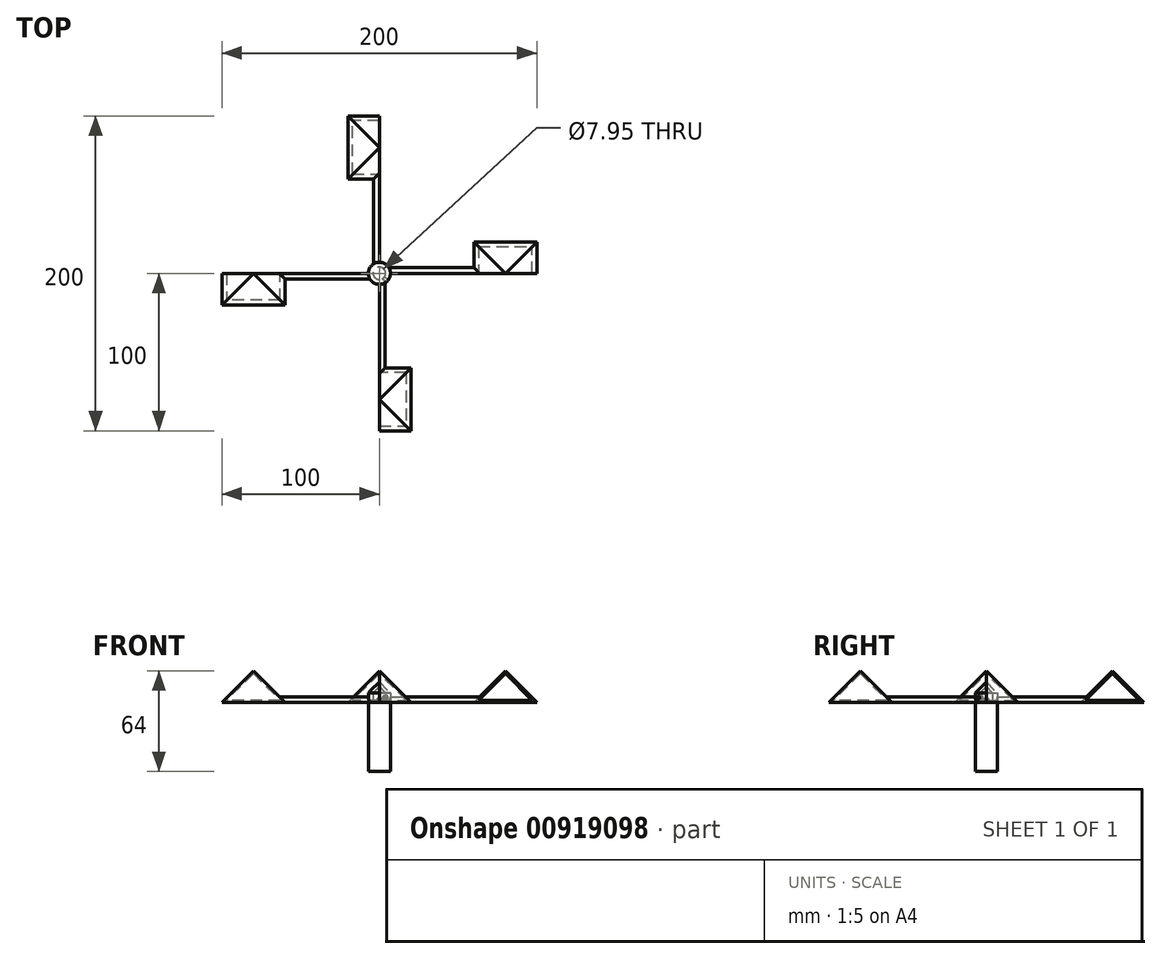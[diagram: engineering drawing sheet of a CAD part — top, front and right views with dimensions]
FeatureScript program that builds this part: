
annotation { "Feature Type Name" : "Feature", "Feature Type Description" : "" }
export const myFeature = defineFeature(function(context is Context, id is Id, definition is map)
    precondition{}
    {
        {
            var Q0;
            Q0=qCreatedBy(makeId("Front.planeOp"),FACE);
            var sketch = newSketch(context, id + "F0", { "sketchPlane" : qUnion([Q0])});
            skLineSegment(sketch, "E0.bottom", {"start": v(3.98, 0) * mm, "end": v(7, 0) * mm});
            skLineSegment(sketch, "E0.top", {"start": v(3.97, 6) * mm, "end": v(7, 6) * mm});
            skLineSegment(sketch, "E0.left", {"start": v(3.98, 0) * mm, "end": v(3.97, 6) * mm});
            skLineSegment(sketch, "E0.right", {"start": v(7, 0) * mm, "end": v(7, 6) * mm});
            skLineSegment(sketch, "E1", {"start": v(0, 0) * mm, "end": v(0, 6) * mm, "construction": true});
            skLineSegment(sketch, "E2.bottom", {"start": v(3.97, 0) * mm, "end": v(60, 0) * mm});
            skLineSegment(sketch, "E2.top", {"start": v(3.97, 3.6) * mm, "end": v(60, 3.6) * mm});
            skLineSegment(sketch, "E2.left", {"start": v(3.98, 0) * mm, "end": v(3.98, 3.6) * mm});
            skLineSegment(sketch, "E2.right", {"start": v(60, 0) * mm, "end": v(60, 3.6) * mm});
            skLineSegment(sketch, "E3.bottom", {"start": v(100, -20) * mm, "end": v(60, -20) * mm});
            skLineSegment(sketch, "E3.top", {"start": v(100, 20) * mm, "end": v(60, 20) * mm});
            skLineSegment(sketch, "E3.left", {"start": v(100, -20) * mm, "end": v(100, 20) * mm});
            skLineSegment(sketch, "E3.right", {"start": v(60, -20) * mm, "end": v(60, 20) * mm});
            skPoint(sketch, "E3.middle", {"position": v(80, 0) * mm});
            skLineSegment(sketch, "E4", {"start": v(60, 0) * mm, "end": v(100, 0) * mm});
            skLineSegment(sketch, "E5", {"start": v(60, 0) * mm, "end": v(63.6, 3.6) * mm});
            skLineSegment(sketch, "E6", {"start": v(63.6, 3.6) * mm, "end": v(60, 3.6) * mm});
            skLineSegment(sketch, "E7", {"start": v(3.97, 6) * mm, "end": v(0, 9.97) * mm});
            skLineSegment(sketch, "E8", {"start": v(0, 9.97) * mm, "end": v(0, 13) * mm});
            skLineSegment(sketch, "E9", {"start": v(0, 13) * mm, "end": v(7, 6) * mm});
            skSolve(sketch);
        }
        {
            var Q0;
            {var subQ2=sQuery(id+"F0.wireOp",EDGE,"E3.top");Q0=makeQuery(id+"F0.imprint","IMPRINT",FACE,{"disambiguationData":[TD([[makeQuery(id+"F0.imprint","IMPRINT",EDGE,{"derivedFrom":subQ2}),1.0]])]});}
            var Q1;
            Q1=makeQuery(id+"F0.imprint","IMPRINT",FACE,{"disambiguationData":[TD([[makeQuery(id+"F0.imprint","IMPRINT",EDGE,{"derivedFrom":sQuery(id+"F0.wireOp",EDGE,"E2.right")}),-1.0]])]});
            extrude(context, id + "F1", {"entities" : qUnion([Q0, Q1]), "oppositeDirection" : true, "depth" : 20 * mm, "offsetDistance" : 25 * mm});
        }
        {
            var Q0;
            Q0=makeQuery(id+"F1.opExtrude","SWEPT_EDGE",EDGE,{"disambiguationData":[OSD([sQuery(id+"F0.wireOp",EDGE,"E3.top"),sQuery(id+"F0.wireOp",EDGE,"E3.right")])]});
            var Q1;
            Q1=makeQuery(id+"F1.opExtrude","CAP_EDGE",EDGE,{"disambiguationData":[OSD([sQuery(id+"F0.wireOp",EDGE,"E3.top")])],"isStart":false});
            var Q2;
            Q2=makeQuery(id+"F1.opExtrude","SWEPT_EDGE",EDGE,{"disambiguationData":[OSD([sQuery(id+"F0.wireOp",EDGE,"E3.top"),sQuery(id+"F0.wireOp",EDGE,"E3.left")])]});
            chamfer(context, id + "F2", {"entities" : qUnion([Q0, Q1, Q2]), "width" : 20 * mm, "tangentPropagation" : true});
        }
        {
            var Q0;
            Q0=makeQuery(id+"F1.opExtrude","CAP_FACE",FACE,{"disambiguationData":[OSD([sQuery(id+"F0.wireOp",EDGE,"E2.right"),sQuery(id+"F0.wireOp",EDGE,"E3.top"),sQuery(id+"F0.wireOp",EDGE,"E3.left"),sQuery(id+"F0.wireOp",EDGE,"E3.right"),sQuery(id+"F0.wireOp",EDGE,"E4")])],"isStart":true});
            shell(context, id + "F3", {"entities" : qUnion([Q0]), "thickness" : 1.2 * mm});
        }
        {
            var Q0;
            {var subQ0=sQuery(id+"F0.wireOp",EDGE,"E2.bottom");Q0=makeQuery(id+"F0.imprint","IMPRINT",FACE,{"disambiguationData":[TD([[makeQuery(id+"F0.imprint","IMPRINT",EDGE,{"derivedFrom":subQ0}),1.0]])]});}
            var Q1;
            Q1=makeQuery(id+"F0.imprint","IMPRINT",FACE,{"disambiguationData":[TD([[makeQuery(id+"F0.imprint","IMPRINT",EDGE,{"derivedFrom":sQuery(id+"F0.wireOp",EDGE,"E2.right")}),-1.0]])]});
            var Q2;
            {var subQ0=sQuery(id+"F0.wireOp",EDGE,"E0.bottom");Q2=makeQuery(id+"F0.imprint","IMPRINT",FACE,{"disambiguationData":[TD([[makeQuery(id+"F0.imprint","IMPRINT",EDGE,{"derivedFrom":subQ0}),1.0]])]});}
            extrude(context, id + "F4", {"entities" : qUnion([Q0, Q1, Q2]), "operationType" : NewBodyOperationType.ADD, "oppositeDirection" : true, "depth" : 5 * mm, "offsetDistance" : 25 * mm});
        }
        {
            var Q0;
            {var subQ0=sQuery(id+"F0.wireOp",EDGE,"E0.top");Q0=makeQuery(id+"F0.imprint","IMPRINT",FACE,{"disambiguationData":[TD([[makeQuery(id+"F0.imprint","IMPRINT",EDGE,{"derivedFrom":subQ0}),-1.0]])]});}
            var Q1;
            {var subQ0=sQuery(id+"F0.wireOp",EDGE,"E0.bottom");Q1=makeQuery(id+"F0.imprint","IMPRINT",FACE,{"disambiguationData":[TD([[makeQuery(id+"F0.imprint","IMPRINT",EDGE,{"derivedFrom":subQ0}),1.0]])]});}
            var Q2;
            Q2=makeQuery(id+"F0.imprint","IMPRINT",FACE,{"disambiguationData":[TD([[makeQuery(id+"F0.imprint","IMPRINT",EDGE,{"derivedFrom":sQuery(id+"F0.wireOp",EDGE,"E0.top")}),1.0]])]});
            var Q3;
            Q3=sQuery(id+"F0.wireOp",EDGE,"E1");
            revolve(context, id + "F5", {"operationType" : NewBodyOperationType.ADD, "surfaceOperationType" : NewSurfaceOperationType.NEW, "entities" : qUnion([Q0, Q1, Q2]), "axis" : qUnion([Q3]), "revolveType" : RevolveType.FULL});
        }
        {
            var Q0;
            Q0=makeQuery(id+"F4.opExtrude","CAP_EDGE",EDGE,{"disambiguationData":[OSD([sQuery(id+"F0.wireOp",EDGE,"E2.top"),sQuery(id+"F0.wireOp",EDGE,"E6")])],"isStart":false});
            chamfer(context, id + "F6", {"entities" : qUnion([Q0]), "width" : 5 * mm, "tangentPropagation" : true});
        }
        {
            var Q0;
            Q0=makeQuery(id+"F1.opExtrude","SWEPT_BODY",BODY,{"disambiguationData":[OSD([sQuery(id+"F0.wireOp",EDGE,"E2.right"),sQuery(id+"F0.wireOp",EDGE,"E3.top"),sQuery(id+"F0.wireOp",EDGE,"E3.left"),sQuery(id+"F0.wireOp",EDGE,"E3.right"),sQuery(id+"F0.wireOp",EDGE,"E4")])]});
            var Q1;
            Q1=sQuery(id+"F0.wireOp",EDGE,"E1");
            circularPattern(context, id + "F7", {"operationType" : NewBodyOperationType.ADD, "entities" : qUnion([Q0]), "axis" : qUnion([Q1]), "angle" : 360 * degree, "instanceCount" : 4, "equalSpace" : true});
        }
        {
            var Q0;
            Q0=qCreatedBy(makeId("Front.planeOp"),FACE);
            var Q1;
            Q1=sQuery(id+"F0.wireOp",EDGE,"E1");
            cPlane(context, id + "F8", {"entities" : qUnion([Q0, Q1]), "cplaneType" : CPlaneType.LINE_ANGLE, "offset" : 25 * mm, "angle" : 45 * degree, "width" : 150 * mm, "height" : 150 * mm});
        }
        {
            var Q0;
            Q0=qCreatedBy(id+"F8.planeOp",FACE);
            var sketch = newSketch(context, id + "F9", { "sketchPlane" : qUnion([Q0])});
            skCircle(sketch, "E10", {"center": v(0, 3) * mm, "radius": 1 * mm});
            skSolve(sketch);
        }
        {
            var Q0;
            Q0=makeQuery(id+"F9.imprint","IMPRINT",FACE,{"disambiguationData":[TD([[makeQuery(id+"F9.imprint","IMPRINT",EDGE,{"derivedFrom":sQuery(id+"F9.wireOp",EDGE,"E10")}),1.0]])]});
            extrude(context, id + "F10", {"entities" : qUnion([Q0]), "operationType" : NewBodyOperationType.REMOVE, "endBound" : BoundingType.THROUGH_ALL, "oppositeDirection" : true, "depth" : 25 * mm, "offsetDistance" : 25 * mm});
        }
        {
            var Q0;
            Q0=qCreatedBy(makeId("Front.planeOp"),FACE);
            var sketch = newSketch(context, id + "F11", { "sketchPlane" : qUnion([Q0])});
            skLineSegment(sketch, "E11", {"start": v(0, 6) * mm, "end": v(3.97, 6) * mm});
            skLineSegment(sketch, "E12", {"start": v(3.98, 6) * mm, "end": v(3.98, 0) * mm});
            skLineSegment(sketch, "E13", {"start": v(3.98, 0) * mm, "end": v(7, 0) * mm});
            skLineSegment(sketch, "E14", {"start": v(7, 0) * mm, "end": v(7, -44) * mm});
            skLineSegment(sketch, "E15", {"start": v(7, -44) * mm, "end": v(0, -44) * mm});
            skLineSegment(sketch, "E16", {"start": v(0, -44) * mm, "end": v(0, 6) * mm});
            skSolve(sketch);
        }
        {
            var Q0;
            Q0=makeQuery(id+"F11.imprint","IMPRINT",FACE,{"disambiguationData":[TD([[makeQuery(id+"F11.imprint","IMPRINT",EDGE,{"derivedFrom":sQuery(id+"F11.wireOp",EDGE,"E11")}),-1.0]])]});
            var Q1;
            Q1=sQuery(id+"F11.wireOp",EDGE,"E16");
            revolve(context, id + "F12", {"surfaceOperationType" : NewSurfaceOperationType.NEW, "entities" : qUnion([Q0]), "axis" : qUnion([Q1]), "revolveType" : RevolveType.FULL});
        }
    });
